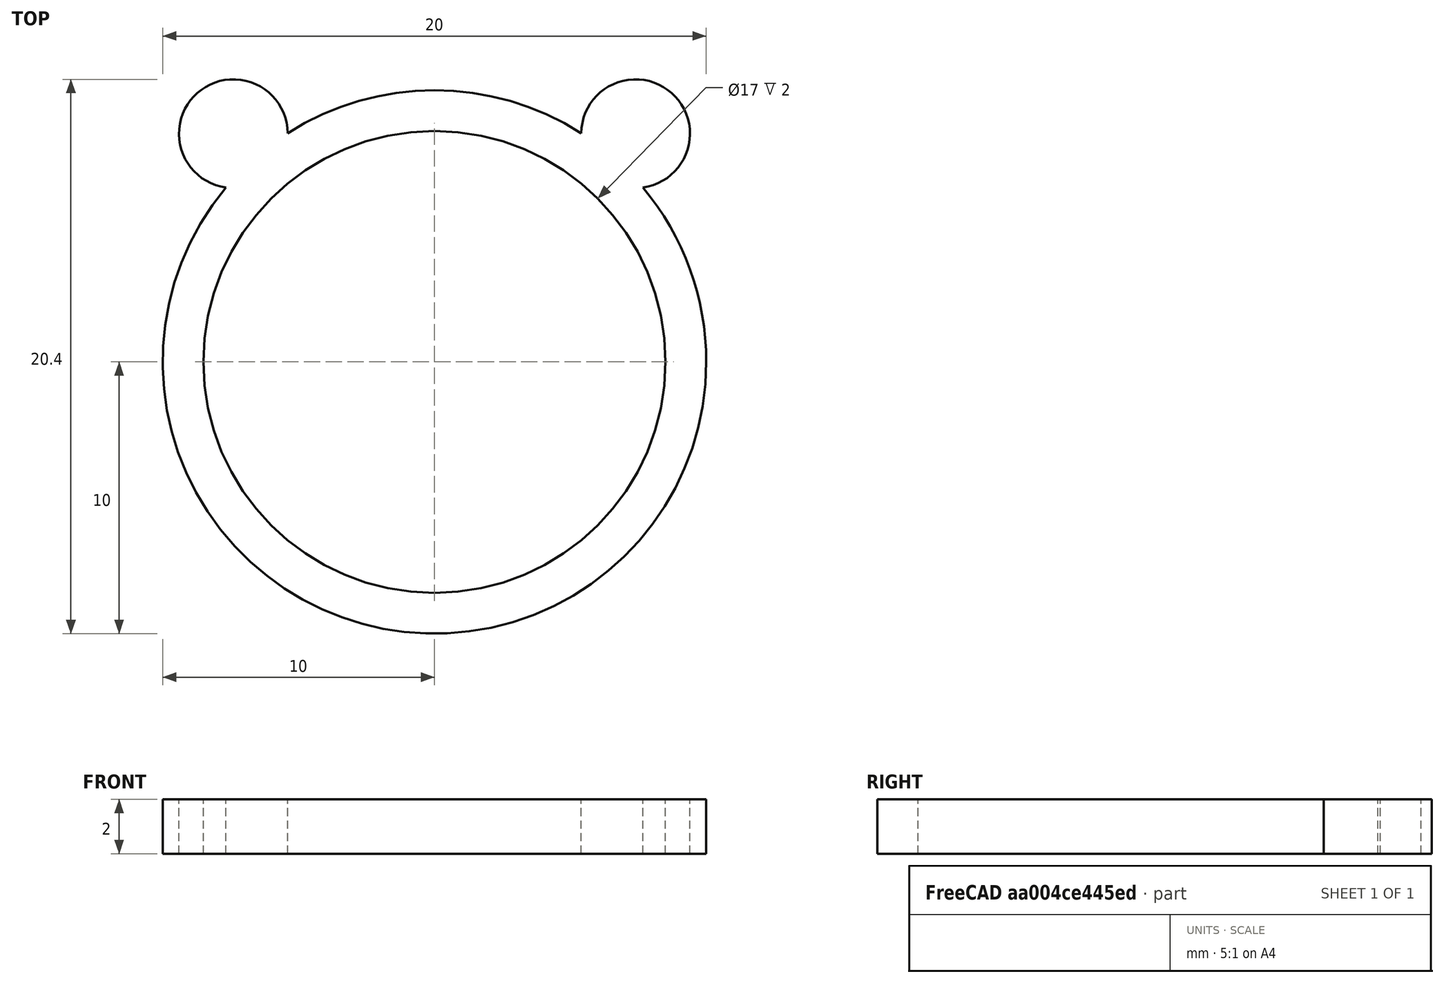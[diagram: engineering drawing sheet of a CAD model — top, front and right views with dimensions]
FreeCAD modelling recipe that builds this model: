
FCSTD DOCUMENT  (FreeCAD 0.17R13217 (Git))
Label: anillo-oso-fc17
License: All rights reserved
LicenseURL: http://en.wikipedia.org/wiki/All_rights_reserved
objects: Part::Cylinder×3, Part::MultiFuse×2, Part::Cut×1, Part::Mirroring×1
note: 7 computed .brp shape members not serialized (recipe doc carries the construction recipe); baked Part::Feature solids carry a one-line shape summary decoded from their .brp

FEATURE [Part::Cylinder] Cylinder  label="Cilindro"
  Angle = 360
  AttacherType = Attacher::AttachEngine3D
  Height = 2
  Radius = 10
FEATURE [Part::Cylinder] Cylinder001  label="Cilindro001"
  Angle = 360
  AttacherType = Attacher::AttachEngine3D
  Height = 10
  Placement = pos=(0,0,-4) rot=(0,0,1;0rad)
  Radius = 8.5
FEATURE [Part::Cut] Cut
  Base = -> Cylinder
  Refine = true
  Tool = -> Cylinder001
FEATURE [Part::Cylinder] Cylinder002  label="Oreja-izquierda"
  Angle = 360
  AttacherType = Attacher::AttachEngine3D
  Height = 2
  Placement = pos=(-7.4,8.4,0) rot=(0,0,1;0rad)
  Radius = 2
FEATURE [Part::Mirroring] Part__Mirroring  label="Oreja-izquierda (Mirror #1)"
  Base = (0,0,0)
  Normal = (1,0,0)
  Source = -> Cylinder002
FEATURE [Part::MultiFuse] Fusion
  Refine = true
  Shapes = -> [Cylinder002,Part__Mirroring]
FEATURE [Part::MultiFuse] Fusion001  label="Anillo-osito"
  Refine = true
  Shapes = -> [Fusion,Cut]
